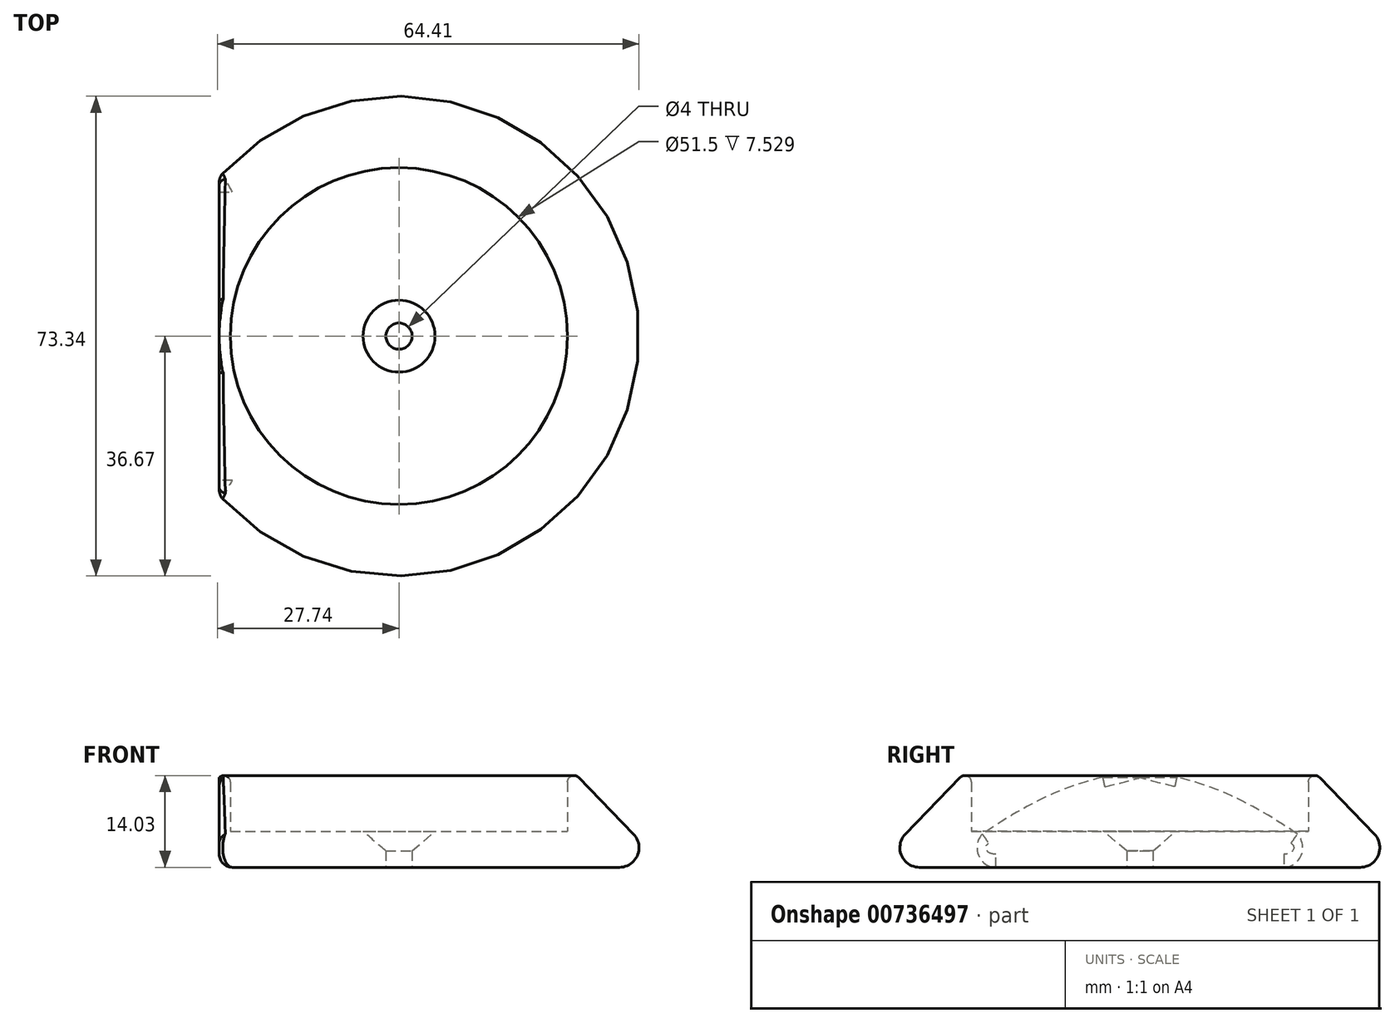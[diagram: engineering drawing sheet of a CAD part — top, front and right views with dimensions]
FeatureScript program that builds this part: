
annotation { "Feature Type Name" : "Feature", "Feature Type Description" : "" }
export const myFeature = defineFeature(function(context is Context, id is Id, definition is map)
    precondition{}
    {
        {
            var Q0;
            Q0=qCreatedBy(makeId("Front.planeOp"),FACE);
            var sketch = newSketch(context, id + "F0", { "sketchPlane" : qUnion([Q0])});
            skLineSegment(sketch, "E0", {"start": v(0, 0) * mm, "end": v(-2, 0) * mm});
            skLineSegment(sketch, "E1", {"start": v(-2, 0) * mm, "end": v(-2, 2.5) * mm});
            skLineSegment(sketch, "E2", {"start": v(-2, 2.5) * mm, "end": v(-5.5, 2.5) * mm});
            skLineSegment(sketch, "E3", {"start": v(-5.5, 2.5) * mm, "end": v(-5.5, 5.5) * mm});
            skLineSegment(sketch, "E4", {"start": v(0, 0) * mm, "end": v(-25.75, 0) * mm});
            skPoint(sketch, "E4.endSnap0", {"position": v(-1, 0) * mm});
            skLineSegment(sketch, "E5", {"start": v(-25.75, 0) * mm, "end": v(-33.67, 0) * mm});
            skLineSegment(sketch, "E6", {"start": v(-35.83, 5.09) * mm, "end": v(-27.47, 13.72) * mm});
            skLineSegment(sketch, "E7", {"start": v(-25.75, 13.03) * mm, "end": v(-25.75, 5.5) * mm});
            skLineSegment(sketch, "E8", {"start": v(-25.75, 5.5) * mm, "end": v(-5.5, 5.5) * mm});
            skLineSegment(sketch, "E9", {"start": v(-5.5, 5.5) * mm, "end": v(-2, 2.5) * mm});
            skPoint(sketch, "E10.visualSharp", {"position": v(-40.75, 0) * mm});
            skArc(sketch, "E10.filletArc", {"start": v(-35.83, 5.09) * mm, "mid": v(-36.43, 1.83) * mm, "end": v(-33.67, 0) * mm});
            skPoint(sketch, "E11.visualSharp", {"position": v(-25.75, 15.5) * mm});
            skArc(sketch, "E11.filletArc", {"start": v(-25.75, 13.03) * mm, "mid": v(-26.37, 13.96) * mm, "end": v(-27.47, 13.72) * mm});
            skLineSegment(sketch, "E12", {"start": v(0, 0) * mm, "end": v(0, 2.64) * mm});
            skLineSegment(sketch, "E13", {"start": v(-27.47, 13.72) * mm, "end": v(-27.47, 0) * mm});
            skLineSegment(sketch, "E14", {"start": v(-27.47, 0) * mm, "end": v(-40.75, 0) * mm});
            skLineSegment(sketch, "E15", {"start": v(-40.75, 0) * mm, "end": v(-40.75, 13.72) * mm});
            skLineSegment(sketch, "E16", {"start": v(-40.75, 13.72) * mm, "end": v(-27.47, 13.72) * mm});
            skSolve(sketch);
        }
        {
            var Q0;
            {var subQ1=sQuery(id+"F0.wireOp",EDGE,"E1");Q0=makeQuery(id+"F0.imprint","IMPRINT",FACE,{"disambiguationData":[TD([[makeQuery(id+"F0.imprint","IMPRINT",EDGE,{"derivedFrom":subQ1}),1.0]])]});}
            var Q1;
            Q1=makeQuery(id+"F0.imprint","IMPRINT",FACE,{"disambiguationData":[TD([[makeQuery(id+"F0.imprint","IMPRINT",EDGE,{"derivedFrom":sQuery(id+"F0.wireOp",EDGE,"E2")}),-1.0]])]});
            var Q2;
            Q2=makeQuery(id+"F0.imprint","IMPRINT",FACE,{"disambiguationData":[TD([[makeQuery(id+"F0.imprint","IMPRINT",EDGE,{"derivedFrom":sQuery(id+"F0.wireOp",EDGE,"E6")}),-1.0]])]});
            var Q3;
            Q3=sQuery(id+"F0.wireOp",EDGE,"E12");
            revolve(context, id + "F1", {"surfaceOperationType" : NewSurfaceOperationType.NEW, "entities" : qUnion([Q0, Q1, Q2]), "axis" : qUnion([Q3]), "revolveType" : RevolveType.FULL});
        }
        {
            var Q0;
            Q0=makeQuery(id+"F0.imprint","IMPRINT",FACE,{"disambiguationData":[TD([[makeQuery(id+"F0.imprint","IMPRINT",EDGE,{"derivedFrom":sQuery(id+"F0.wireOp",EDGE,"E6")}),-1.0]])]});
            var Q1;
            Q1=makeQuery(id+"F0.imprint","IMPRINT",FACE,{"disambiguationData":[TD([[makeQuery(id+"F0.imprint","IMPRINT",EDGE,{"derivedFrom":sQuery(id+"F0.wireOp",EDGE,"E6")}),1.0]])]});
            extrude(context, id + "F2", {"entities" : qUnion([Q0, Q1]), "operationType" : NewBodyOperationType.REMOVE, "endBound" : BoundingType.UP_TO_NEXT, "oppositeDirection" : true, "depth" : 25 * mm, "offsetDistance" : 25 * mm});
        }
        {
            var Q0;
            Q0=makeQuery(id+"F2.boolean.opBoolean","COPY",FACE,{"derivedFrom":makeQuery(id+"F2.opExtrude","CAP_FACE",FACE,{"disambiguationData":[OSD([sQuery(id+"F0.wireOp",EDGE,"E13"),sQuery(id+"F0.wireOp",EDGE,"E14"),sQuery(id+"F0.wireOp",EDGE,"E15"),sQuery(id+"F0.wireOp",EDGE,"E16")])],"isStart":true})});
            extrude(context, id + "F3", {"entities" : qUnion([Q0]), "operationType" : NewBodyOperationType.REMOVE, "endBound" : BoundingType.UP_TO_NEXT, "oppositeDirection" : true, "depth" : 25 * mm, "offsetDistance" : 25 * mm});
        }
        {
            var Q0;
            Q0=makeQuery(id+"F2.boolean.opBoolean","COPY",EDGE,{"derivedFrom":makeQuery(id+"F2.opExtrude","TWEAK_EDGE",EDGE,{"derivedFrom":[makeQuery(id+"F0.imprint","IMPRINT",EDGE,{"derivedFrom":sQuery(id+"F0.wireOp",EDGE,"E13")}),makeQuery(id+"F1.opRevolve","SWEPT_FACE",FACE,{"disambiguationData":[OSD([sQuery(id+"F0.wireOp",EDGE,"E6")])]})]})});
            var Q1;
            Q1=makeQuery(id+"F1.opRevolve","SWEPT_FACE",FACE,{"disambiguationData":[OSD([sQuery(id+"F0.wireOp",EDGE,"E10.filletArc")])]});
            fillet(context, id + "F4", {"entities" : qUnion([Q0, Q1]), "radius" : 2 * mm, "tangentPropagation" : true, "allowEdgeOverflow" : false});
        }
    });
